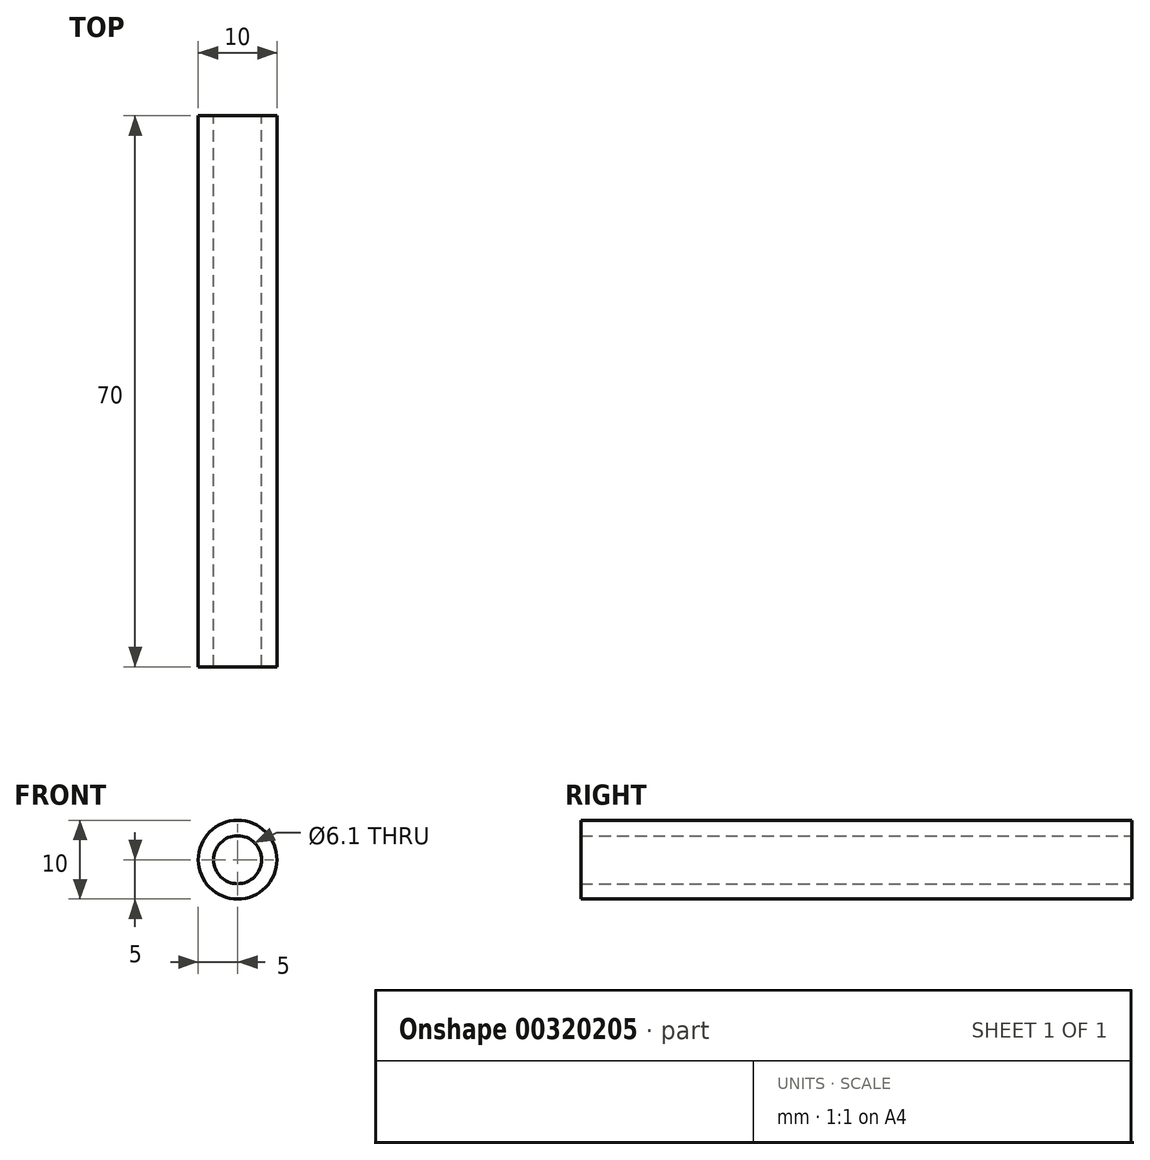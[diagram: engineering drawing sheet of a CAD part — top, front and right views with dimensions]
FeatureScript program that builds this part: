
annotation { "Feature Type Name" : "Feature", "Feature Type Description" : "" }
export const myFeature = defineFeature(function(context is Context, id is Id, definition is map)
    precondition{}
    {
        {
            var Q0;
            Q0=qCreatedBy(makeId("Front.planeOp"),FACE);
            var sketch = newSketch(context, id + "F0", { "sketchPlane" : qUnion([Q0])});
            skCircle(sketch, "E0", {"center": v(0, 0) * mm, "radius": 5 * mm});
            skCircle(sketch, "E1", {"center": v(0, 0) * mm, "radius": 3.05 * mm});
            skSolve(sketch);
        }
        {
            var Q0;
            Q0=qSketchRegion(id+"F0",true);
            extrude(context, id + "F1", {"entities" : qUnion([Q0]), "endBound" : BoundingType.SYMMETRIC, "depth" : 70 * mm});
        }
    });
